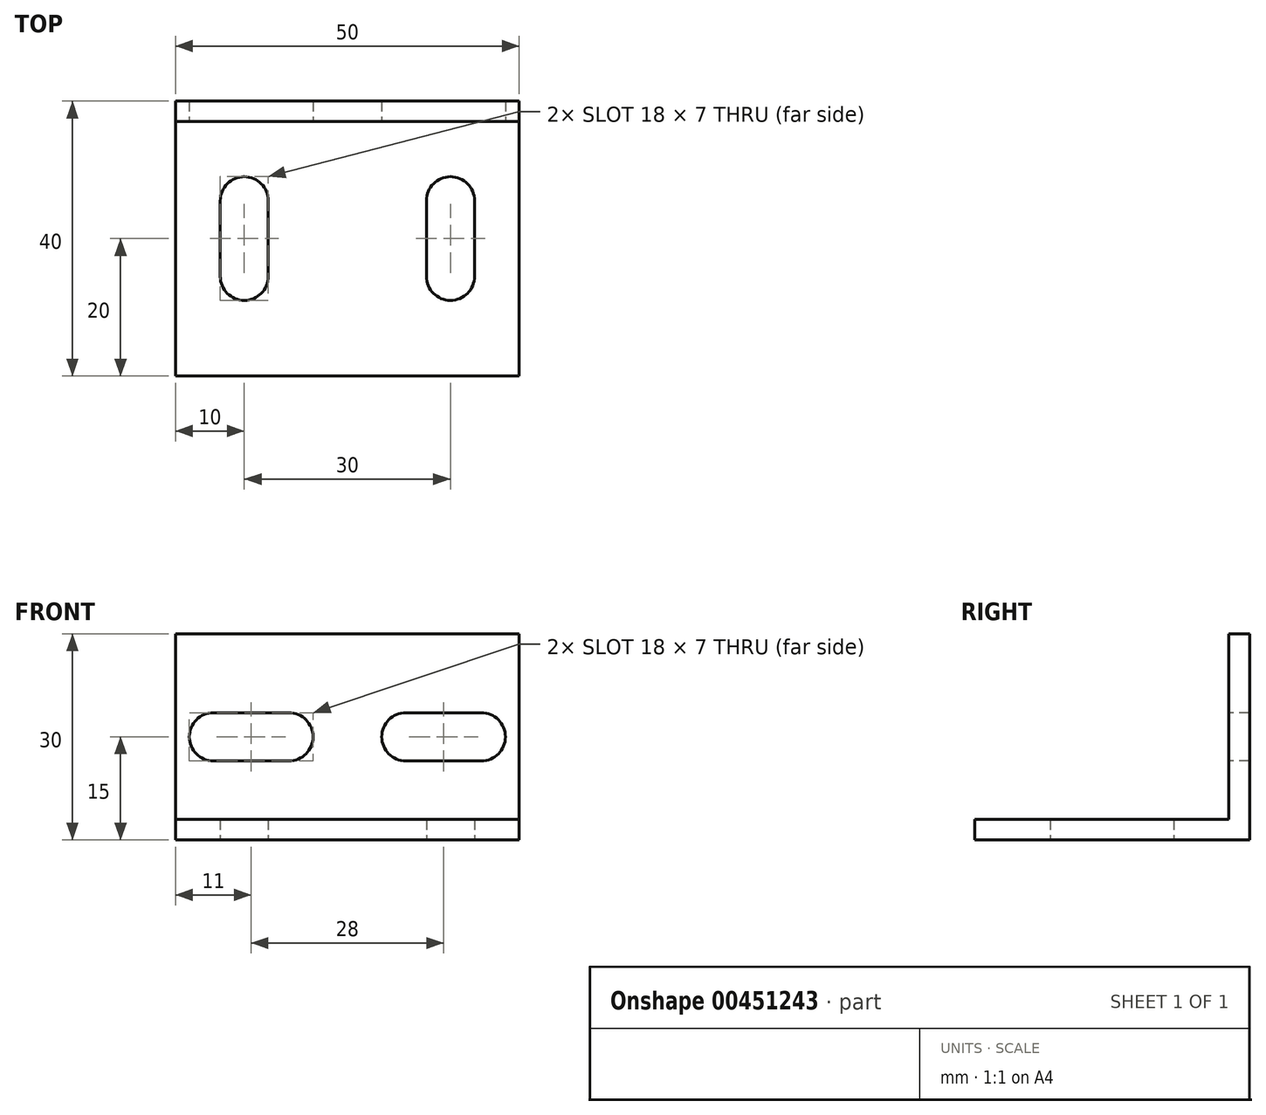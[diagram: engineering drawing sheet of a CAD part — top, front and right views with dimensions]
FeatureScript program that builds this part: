
annotation { "Feature Type Name" : "Feature", "Feature Type Description" : "" }
export const myFeature = defineFeature(function(context is Context, id is Id, definition is map)
    precondition{}
    {
        {
            var Q0;
            Q0=qCreatedBy(makeId("Top.planeOp"),FACE);
            var sketch = newSketch(context, id + "F0", { "sketchPlane" : qUnion([Q0])});
            skLineSegment(sketch, "E0.bottom", {"start": v(25, 0) * mm, "end": v(-25, 0) * mm});
            skLineSegment(sketch, "E0.top", {"start": v(25, 40) * mm, "end": v(-25, 40) * mm});
            skLineSegment(sketch, "E0.left", {"start": v(25, 0) * mm, "end": v(25, 40) * mm});
            skLineSegment(sketch, "E0.right", {"start": v(-25, 0) * mm, "end": v(-25, 40) * mm});
            skLineSegment(sketch, "E1.bottom", {"start": v(-11.5, 14.5) * mm, "end": v(-18.5, 14.5) * mm, "construction": true});
            skLineSegment(sketch, "E1.top", {"start": v(-11.5, 25.5) * mm, "end": v(-18.5, 25.5) * mm, "construction": true});
            skLineSegment(sketch, "E1.left", {"start": v(-11.5, 14.5) * mm, "end": v(-11.5, 25.5) * mm});
            skLineSegment(sketch, "E1.right", {"start": v(-18.5, 14.5) * mm, "end": v(-18.5, 25.5) * mm});
            skPoint(sketch, "E1.middle", {"position": v(-15, 20) * mm});
            skArc(sketch, "E2", {"start": v(-11.5, 25.5) * mm, "mid": v(-15, 29) * mm, "end": v(-18.5, 25.5) * mm});
            skArc(sketch, "E3", {"start": v(-18.5, 14.5) * mm, "mid": v(-15, 11) * mm, "end": v(-11.5, 14.5) * mm});
            skLineSegment(sketch, "E4", {"start": v(0, 0) * mm, "end": v(0, -23) * mm, "construction": true});
            skLineSegment(sketch, "E5.MirrorCS", {"start": v(11.5, 25.5) * mm, "end": v(18.5, 25.5) * mm, "construction": true});
            skLineSegment(sketch, "E6.MirrorCS", {"start": v(11.5, 14.5) * mm, "end": v(18.5, 14.5) * mm, "construction": true});
            skArc(sketch, "E7.MirrorCS", {"start": v(11.5, 25.5) * mm, "mid": v(15, 29) * mm, "end": v(18.5, 25.5) * mm});
            skLineSegment(sketch, "E8.MirrorCS", {"start": v(11.5, 14.5) * mm, "end": v(11.5, 25.5) * mm});
            skPoint(sketch, "E9.MirrorP", {"position": v(15, 20) * mm});
            skArc(sketch, "E10.MirrorCS", {"start": v(18.5, 14.5) * mm, "mid": v(15, 11) * mm, "end": v(11.5, 14.5) * mm});
            skLineSegment(sketch, "E11.MirrorCS", {"start": v(18.5, 14.5) * mm, "end": v(18.5, 25.5) * mm});
            skSolve(sketch);
        }
        {
            var Q0;
            Q0=qSketchRegion(id+"F0",true);
            extrude(context, id + "F1", {"entities" : qUnion([Q0]), "depth" : 3 * mm, "offsetDistance" : 25 * mm});
        }
        {
            var Q0;
            Q0=makeQuery(id+"F1.opExtrude","CAP_FACE",FACE,{"disambiguationData":[OSD([sQuery(id+"F0.wireOp",EDGE,"E0.bottom"),sQuery(id+"F0.wireOp",EDGE,"E0.top"),sQuery(id+"F0.wireOp",EDGE,"E0.left"),sQuery(id+"F0.wireOp",EDGE,"E0.right")])],"isStart":false});
            var sketch = newSketch(context, id + "F2", { "sketchPlane" : qUnion([Q0])});
            skLineSegment(sketch, "E12.bottom", {"start": v(-25, 40) * mm, "end": v(25, 40) * mm});
            skLineSegment(sketch, "E12.top", {"start": v(-25, 37) * mm, "end": v(25, 37) * mm});
            skLineSegment(sketch, "E12.left", {"start": v(-25, 40) * mm, "end": v(-25, 37) * mm});
            skLineSegment(sketch, "E12.right", {"start": v(25, 40) * mm, "end": v(25, 37) * mm});
            skSolve(sketch);
        }
        {
            var Q0;
            Q0=qSketchRegion(id+"F2",true);
            extrude(context, id + "F3", {"entities" : qUnion([Q0]), "operationType" : NewBodyOperationType.ADD, "depth" : 27 * mm, "offsetDistance" : 25 * mm});
        }
        {
            var Q0;
            Q0=makeQuery(id+"F3.opExtrude","SWEPT_FACE",FACE,{"disambiguationData":[OSD([sQuery(id+"F2.wireOp",EDGE,"E12.top")])]});
            var sketch = newSketch(context, id + "F4", { "sketchPlane" : qUnion([Q0])});
            skLineSegment(sketch, "E13.bottom", {"start": v(-8.5, 11.5) * mm, "end": v(-19.5, 11.5) * mm});
            skLineSegment(sketch, "E13.top", {"start": v(-8.5, 18.5) * mm, "end": v(-19.5, 18.5) * mm});
            skLineSegment(sketch, "E13.left", {"start": v(-8.5, 11.5) * mm, "end": v(-8.5, 18.5) * mm, "construction": true});
            skLineSegment(sketch, "E13.right", {"start": v(-19.5, 11.5) * mm, "end": v(-19.5, 18.5) * mm, "construction": true});
            skPoint(sketch, "E13.middle", {"position": v(-14, 15) * mm});
            skArc(sketch, "E14", {"start": v(-19.5, 18.5) * mm, "mid": v(-23, 15) * mm, "end": v(-19.5, 11.5) * mm});
            skArc(sketch, "E15", {"start": v(-8.5, 11.5) * mm, "mid": v(-5, 15) * mm, "end": v(-8.5, 18.5) * mm});
            skLineSegment(sketch, "E16", {"start": v(0, 0) * mm, "end": v(0, -17.2) * mm, "construction": true});
            skLineSegment(sketch, "E17.MirrorCS", {"start": v(8.5, 11.5) * mm, "end": v(8.5, 18.5) * mm, "construction": true});
            skLineSegment(sketch, "E18.MirrorCS", {"start": v(19.5, 11.5) * mm, "end": v(19.5, 18.5) * mm, "construction": true});
            skArc(sketch, "E19.MirrorCS", {"start": v(8.5, 11.5) * mm, "mid": v(5, 15) * mm, "end": v(8.5, 18.5) * mm});
            skLineSegment(sketch, "E20.MirrorCS", {"start": v(8.5, 18.5) * mm, "end": v(19.5, 18.5) * mm});
            skArc(sketch, "E21.MirrorCS", {"start": v(19.5, 18.5) * mm, "mid": v(23, 15) * mm, "end": v(19.5, 11.5) * mm});
            skLineSegment(sketch, "E22.MirrorCS", {"start": v(8.5, 11.5) * mm, "end": v(19.5, 11.5) * mm});
            skPoint(sketch, "E23.MirrorP", {"position": v(14, 15) * mm});
            skSolve(sketch);
        }
        {
            var Q0;
            Q0=qSketchRegion(id+"F4",true);
            extrude(context, id + "F5", {"entities" : qUnion([Q0]), "operationType" : NewBodyOperationType.REMOVE, "oppositeDirection" : true, "depth" : 3 * mm, "offsetDistance" : 25 * mm});
        }
    });
